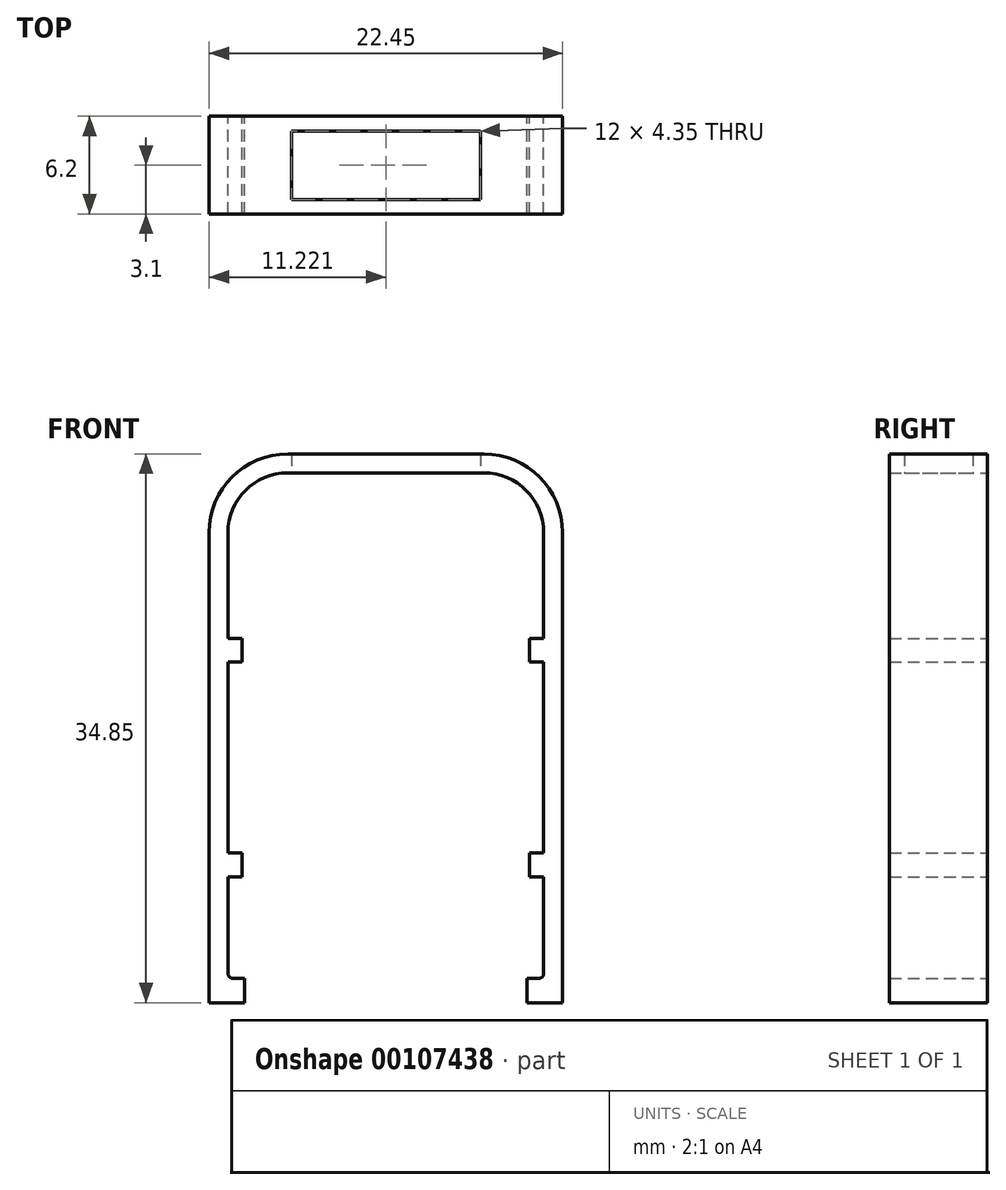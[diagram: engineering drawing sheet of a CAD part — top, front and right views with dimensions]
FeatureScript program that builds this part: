
annotation { "Feature Type Name" : "Feature", "Feature Type Description" : "" }
export const myFeature = defineFeature(function(context is Context, id is Id, definition is map)
    precondition{}
    {
        {
            var Q0;
            Q0=qCreatedBy(makeId("Front.planeOp"),FACE);
            var sketch = newSketch(context, id + "F0", { "sketchPlane" : qUnion([Q0])});
            skLineSegment(sketch, "E0.bottom", {"start": v(-46.55, 25.76) * mm, "end": v(33.45, 25.76) * mm});
            skLineSegment(sketch, "E0.top", {"start": v(-46.55, -24.24) * mm, "end": v(33.45, -24.24) * mm});
            skLineSegment(sketch, "E0.left", {"start": v(-51.55, 20.76) * mm, "end": v(-51.55, -19.24) * mm});
            skLineSegment(sketch, "E0.right", {"start": v(38.45, 20.76) * mm, "end": v(38.45, -19.24) * mm});
            skArc(sketch, "E1.filletArc", {"start": v(-46.55, 25.76) * mm, "mid": v(-50.09, 24.3) * mm, "end": v(-51.55, 20.76) * mm});
            skArc(sketch, "E2.filletArc", {"start": v(38.45, 20.76) * mm, "mid": v(36.98, 24.3) * mm, "end": v(33.45, 25.76) * mm});
            skArc(sketch, "E3.filletArc", {"start": v(33.45, -24.24) * mm, "mid": v(36.98, -22.77) * mm, "end": v(38.45, -19.24) * mm});
            skArc(sketch, "E4.filletArc", {"start": v(-51.55, -19.24) * mm, "mid": v(-50.09, -22.77) * mm, "end": v(-46.55, -24.24) * mm});
            skSolve(sketch);
        }
        {
            var Q0;
            Q0=makeQuery(id+"F0.imprint","IMPRINT",FACE,{"disambiguationData":[TD([[makeQuery(id+"F0.imprint","IMPRINT",EDGE,{"derivedFrom":sQuery(id+"F0.wireOp",EDGE,"E0.bottom")}),-1.0]])]});
            extrude(context, id + "F1", {"entities" : qUnion([Q0]), "depth" : 9.8 * mm});
        }
        {
            var Q0;
            Q0=makeQuery(id+"F1.opExtrude","CAP_FACE",FACE,{"disambiguationData":[OSD([sQuery(id+"F0.wireOp",EDGE,"E0.bottom"),sQuery(id+"F0.wireOp",EDGE,"E0.top"),sQuery(id+"F0.wireOp",EDGE,"E0.left"),sQuery(id+"F0.wireOp",EDGE,"E0.right"),sQuery(id+"F0.wireOp",EDGE,"E1.filletArc"),sQuery(id+"F0.wireOp",EDGE,"E2.filletArc"),sQuery(id+"F0.wireOp",EDGE,"E3.filletArc"),sQuery(id+"F0.wireOp",EDGE,"E4.filletArc")])],"isStart":false});
            shell(context, id + "F2", {"entities" : qUnion([Q0]), "thickness" : 2.5 * mm});
        }
        {
            var Q0;
            {var subQ0=sQuery(id+"F0.wireOp",EDGE,"E0.bottom");Q0=makeQuery(id+"F2.opShell","OFFSET_EDGE",EDGE,{"disambiguationData":[OSD([subQ0]),TDD([makeQuery(id+"F1.opExtrude","CAP_EDGE",EDGE,{"disambiguationData":[OSD([subQ0])],"isStart":true})])]});}
            fillet(context, id + "F3", {"entities" : qUnion([Q0]), "radius" : 5 * mm, "tangentPropagation" : true, "allowEdgeOverflow" : false});
        }
        {
            var Q0;
            {var subQ0=sQuery(id+"F0.wireOp",EDGE,"E0.bottom");Q0=makeQuery(id+"F2.opShell","OFFSET_EDGE",EDGE,{"disambiguationData":[OSD([subQ0]),TDD([makeQuery(id+"F1.opExtrude","CAP_EDGE",EDGE,{"disambiguationData":[OSD([subQ0])],"isStart":false})])]});}
            fillet(context, id + "F4", {"entities" : qUnion([Q0]), "radius" : 5 * mm, "tangentPropagation" : true, "allowEdgeOverflow" : false});
        }
        {
            var Q0;
            Q0=makeQuery(id+"F1.opExtrude","CAP_EDGE",EDGE,{"disambiguationData":[OSD([sQuery(id+"F0.wireOp",EDGE,"E0.bottom")])],"isStart":true});
            fillet(context, id + "F5", {"entities" : qUnion([Q0]), "radius" : 7 * mm, "tangentPropagation" : true, "allowEdgeOverflow" : false});
        }
        {
            var Q0;
            Q0=qCreatedBy(makeId("Front.planeOp"),FACE);
            var sketch = newSketch(context, id + "F6", { "sketchPlane" : qUnion([Q0])});
            skLineSegment(sketch, "E5", {"start": v(38.6, 0) * mm, "end": v(-51.4, 0) * mm, "construction": true});
            skPoint(sketch, "E6", {"position": v(-6.4, 0) * mm});
            skLineSegment(sketch, "E7", {"start": v(-6.4, -35.43) * mm, "end": v(-6.4, 48.54) * mm, "construction": true});
            skCircle(sketch, "E8", {"center": v(-6.4, 0) * mm, "radius": 4.5 * mm});
            skSolve(sketch);
        }
        {
            var Q0;
            Q0=makeQuery(id+"F6.imprint","IMPRINT",FACE,{"disambiguationData":[TD([[makeQuery(id+"F6.imprint","IMPRINT",EDGE,{"derivedFrom":sQuery(id+"F6.wireOp",EDGE,"E8")}),1.0]])]});
            var Q1;
            Q1=sQuery(id+"F6.wireOp",EDGE,"E8");
            extrude(context, id + "F7", {"entities" : qUnion([Q0]), "surfaceEntities" : qUnion([Q1]), "oppositeDirection" : true, "depth" : 130 * mm});
        }
        {
            var Q0;
            Q0=makeQuery(id+"F7.opExtrude","CAP_FACE",FACE,{"disambiguationData":[OSD([sQuery(id+"F6.wireOp",EDGE,"E8")])],"isStart":false});
            shell(context, id + "F8", {"entities" : qUnion([Q0]), "thickness" : 2.5 * mm});
        }
        {
            var Q0;
            Q0=makeQuery(id+"F7.opExtrude","SWEPT_BODY",BODY,{"disambiguationData":[OSD([sQuery(id+"F6.wireOp",EDGE,"E8")])]});
            deleteBodies(context, id + "F9", {"entities" : qUnion([Q0])});
        }
        {
            var Q0;
            Q0=makeQuery(id+"F1.opExtrude","SWEPT_BODY",BODY,{"disambiguationData":[OSD([sQuery(id+"F0.wireOp",EDGE,"E0.bottom"),sQuery(id+"F0.wireOp",EDGE,"E0.top"),sQuery(id+"F0.wireOp",EDGE,"E0.left"),sQuery(id+"F0.wireOp",EDGE,"E0.right"),sQuery(id+"F0.wireOp",EDGE,"E1.filletArc"),sQuery(id+"F0.wireOp",EDGE,"E2.filletArc"),sQuery(id+"F0.wireOp",EDGE,"E3.filletArc"),sQuery(id+"F0.wireOp",EDGE,"E4.filletArc")])]});
            deleteBodies(context, id + "F10", {"entities" : qUnion([Q0])});
        }
        {
            var Q0;
            Q0=qCreatedBy(makeId("Front.planeOp"),FACE);
            var sketch = newSketch(context, id + "F11", { "sketchPlane" : qUnion([Q0])});
            skLineSegment(sketch, "E9.bottom", {"start": v(-55.87, 46.45) * mm, "end": v(-43.42, 46.45) * mm});
            skLineSegment(sketch, "E9.left", {"start": v(-60.87, 41.45) * mm, "end": v(-60.87, 11.6) * mm});
            skLineSegment(sketch, "E9.right", {"start": v(-38.42, 41.45) * mm, "end": v(-38.42, 11.6) * mm});
            skPoint(sketch, "E10.visualSharp", {"position": v(-60.87, 46.45) * mm});
            skArc(sketch, "E10.filletArc", {"start": v(-55.87, 46.45) * mm, "mid": v(-59.4, 44.98) * mm, "end": v(-60.87, 41.45) * mm});
            skPoint(sketch, "E11.visualSharp", {"position": v(-38.42, 46.45) * mm});
            skArc(sketch, "E11.filletArc", {"start": v(-38.42, 41.45) * mm, "mid": v(-39.89, 44.98) * mm, "end": v(-43.42, 46.45) * mm});
            skLineSegment(sketch, "E12.0", {"start": v(-39.62, 41.45) * mm, "end": v(-39.62, 34.75) * mm});
            skLineSegment(sketch, "E12.1", {"start": v(-59.67, 41.45) * mm, "end": v(-59.67, 34.75) * mm});
            skArc(sketch, "E12.2", {"start": v(-55.87, 45.25) * mm, "mid": v(-58.56, 44.14) * mm, "end": v(-59.67, 41.45) * mm});
            skLineSegment(sketch, "E12.3", {"start": v(-55.87, 45.25) * mm, "end": v(-43.42, 45.25) * mm});
            skArc(sketch, "E12.4", {"start": v(-39.62, 41.45) * mm, "mid": v(-40.74, 44.14) * mm, "end": v(-43.42, 45.25) * mm});
            skLineSegment(sketch, "E13", {"start": v(-60.87, 11.6) * mm, "end": v(-58.62, 11.6) * mm});
            skLineSegment(sketch, "E14", {"start": v(-38.42, 11.6) * mm, "end": v(-40.67, 11.6) * mm});
            skLineSegment(sketch, "E15", {"start": v(-58.62, 11.6) * mm, "end": v(-58.62, 13.15) * mm});
            skLineSegment(sketch, "E16", {"start": v(-40.67, 11.6) * mm, "end": v(-40.67, 13.15) * mm});
            skLineSegment(sketch, "E17", {"start": v(-58.62, 13.15) * mm, "end": v(-59.67, 13.15) * mm});
            skLineSegment(sketch, "E18", {"start": v(-40.67, 13.15) * mm, "end": v(-39.62, 13.15) * mm});
            skLineSegment(sketch, "E19", {"start": v(-59.67, 19.6) * mm, "end": v(-58.77, 19.6) * mm});
            skLineSegment(sketch, "E20", {"start": v(-58.77, 19.6) * mm, "end": v(-58.77, 21.1) * mm});
            skLineSegment(sketch, "E21", {"start": v(-58.77, 21.1) * mm, "end": v(-59.67, 21.1) * mm});
            skLineSegment(sketch, "E22.trimOffspring", {"start": v(-59.67, 19.6) * mm, "end": v(-59.67, 13.15) * mm});
            skLineSegment(sketch, "E23", {"start": v(-39.62, 19.6) * mm, "end": v(-40.52, 19.6) * mm});
            skLineSegment(sketch, "E24", {"start": v(-40.52, 19.6) * mm, "end": v(-40.52, 21.1) * mm});
            skLineSegment(sketch, "E25", {"start": v(-40.52, 21.1) * mm, "end": v(-39.62, 21.1) * mm});
            skLineSegment(sketch, "E26.trimOffspring", {"start": v(-39.62, 19.6) * mm, "end": v(-39.62, 13.15) * mm});
            skLineSegment(sketch, "E27", {"start": v(-59.67, 33.25) * mm, "end": v(-58.77, 33.25) * mm});
            skLineSegment(sketch, "E28", {"start": v(-58.77, 33.25) * mm, "end": v(-58.77, 34.75) * mm});
            skLineSegment(sketch, "E29", {"start": v(-58.77, 34.75) * mm, "end": v(-59.67, 34.75) * mm});
            skLineSegment(sketch, "E30.trimOffspring", {"start": v(-59.67, 33.25) * mm, "end": v(-59.67, 21.1) * mm});
            skLineSegment(sketch, "E31", {"start": v(-39.62, 33.25) * mm, "end": v(-40.52, 33.25) * mm});
            skLineSegment(sketch, "E32", {"start": v(-40.52, 33.25) * mm, "end": v(-40.52, 34.75) * mm});
            skLineSegment(sketch, "E33", {"start": v(-40.52, 34.75) * mm, "end": v(-39.62, 34.75) * mm});
            skLineSegment(sketch, "E34.trimOffspring", {"start": v(-39.62, 33.25) * mm, "end": v(-39.62, 21.1) * mm});
            skSolve(sketch);
        }
        {
            var Q0;
            Q0=makeQuery(id+"F11.imprint","IMPRINT",FACE,{"disambiguationData":[TD([[makeQuery(id+"F11.imprint","IMPRINT",EDGE,{"derivedFrom":sQuery(id+"F11.wireOp",EDGE,"E9.bottom")}),-1.0]])]});
            extrude(context, id + "F12", {"entities" : qUnion([Q0]), "depth" : 6.2 * mm});
        }
        {
            var Q0;
            Q0=makeQuery(id+"F12.opExtrude","SWEPT_EDGE",EDGE,{"disambiguationData":[OSD([sQuery(id+"F11.wireOp",EDGE,"E17"),sQuery(id+"F11.wireOp",EDGE,"E22.trimOffspring")])]});
            fillet(context, id + "F13", {"entities" : qUnion([Q0]), "radius" : .3 * mm, "tangentPropagation" : true, "allowEdgeOverflow" : false});
        }
        {
            var Q0;
            Q0=makeQuery(id+"F12.opExtrude","SWEPT_EDGE",EDGE,{"disambiguationData":[OSD([sQuery(id+"F11.wireOp",EDGE,"E18"),sQuery(id+"F11.wireOp",EDGE,"E26.trimOffspring")])]});
            fillet(context, id + "F14", {"entities" : qUnion([Q0]), "radius" : .3 * mm, "tangentPropagation" : true, "allowEdgeOverflow" : false});
        }
        {
            var Q0;
            Q0=qCreatedBy(makeId("Top.planeOp"),FACE);
            var sketch = newSketch(context, id + "F15", { "sketchPlane" : qUnion([Q0])});
            skLineSegment(sketch, "E35.0", {"start": v(-55.87, -6.2) * mm, "end": v(-55.87, 0) * mm});
            skLineSegment(sketch, "E36.0", {"start": v(-43.42, -6.2) * mm, "end": v(-43.42, 0) * mm});
            skLineSegment(sketch, "E37", {"start": v(-55.87, -3.1) * mm, "end": v(-43.42, -3.1) * mm, "construction": true});
            skLineSegment(sketch, "E38", {"start": v(-49.65, 0) * mm, "end": v(-49.65, -7.03) * mm, "construction": true});
            skPoint(sketch, "E38.startSnap0", {"position": v(-49.65, -3.1) * mm});
            skLineSegment(sketch, "E39.bottom", {"start": v(-55.65, -0.93) * mm, "end": v(-43.65, -0.93) * mm});
            skLineSegment(sketch, "E39.top", {"start": v(-55.65, -5.28) * mm, "end": v(-43.65, -5.28) * mm});
            skLineSegment(sketch, "E39.left", {"start": v(-55.65, -0.93) * mm, "end": v(-55.65, -5.28) * mm});
            skLineSegment(sketch, "E39.right", {"start": v(-43.65, -0.93) * mm, "end": v(-43.65, -5.28) * mm});
            skSolve(sketch);
        }
        {
            var Q0;
            Q0=makeQuery(id+"F15.imprint","IMPRINT",FACE,{"disambiguationData":[TD([[makeQuery(id+"F15.imprint","IMPRINT",EDGE,{"derivedFrom":sQuery(id+"F15.wireOp",EDGE,"E39.bottom")}),-1.0]])]});
            extrude(context, id + "F16", {"entities" : qUnion([Q0]), "operationType" : NewBodyOperationType.REMOVE, "depth" : 67.9 * mm});
        }
    });
